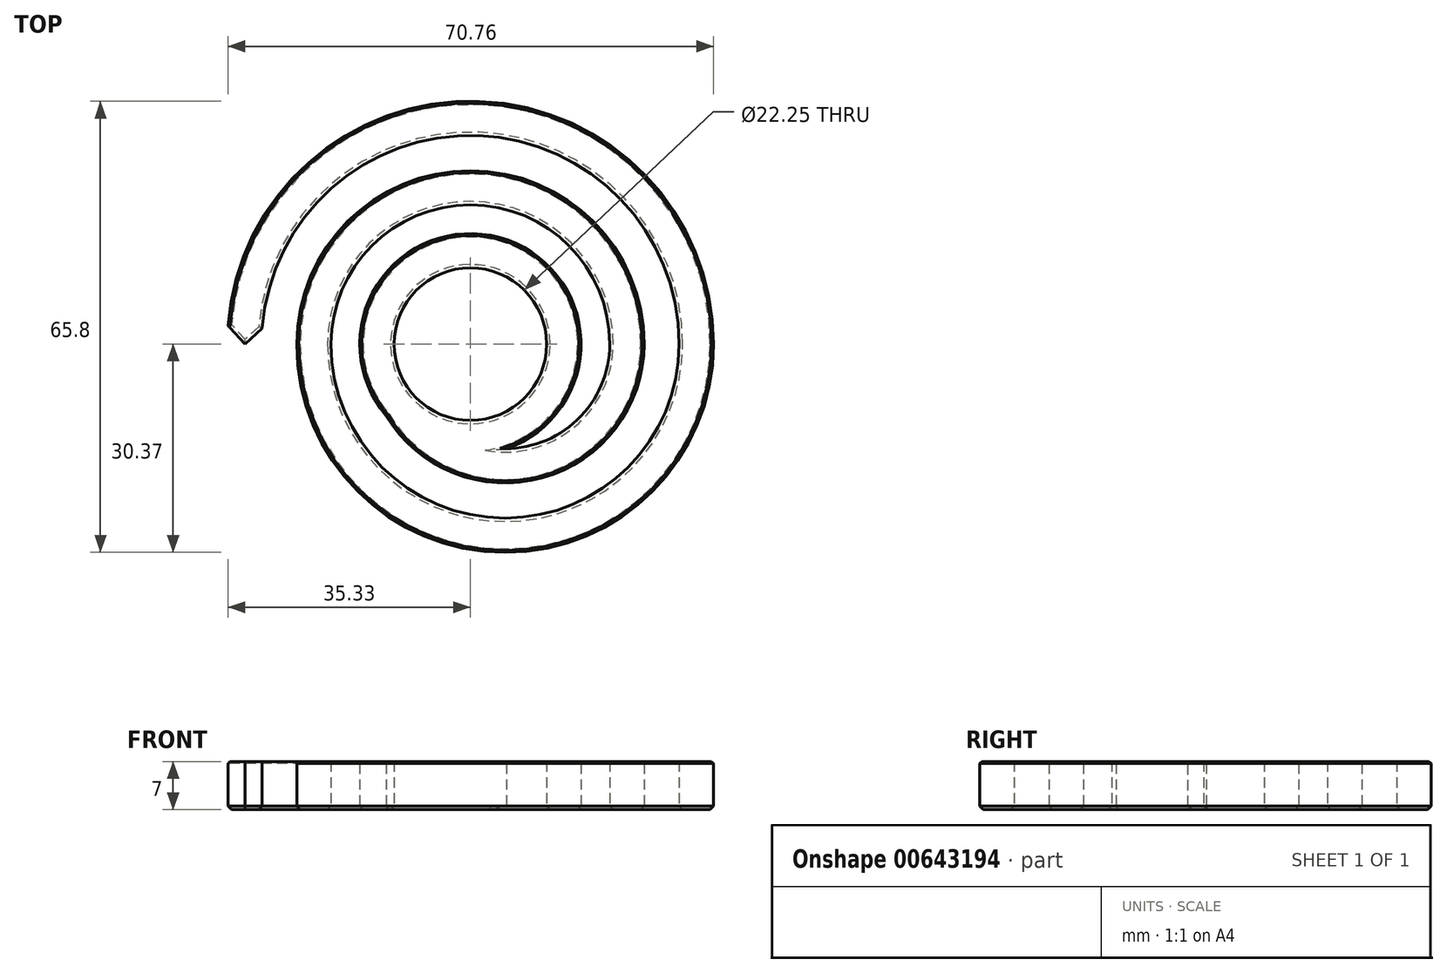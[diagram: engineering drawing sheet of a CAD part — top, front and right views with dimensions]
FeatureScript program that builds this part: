
annotation { "Feature Type Name" : "Feature", "Feature Type Description" : "" }
export const myFeature = defineFeature(function(context is Context, id is Id, definition is map)
    precondition{}
    {
        {
            var Q0;
            Q0=qCreatedBy(makeId("Top.planeOp"),FACE);
            var sketch = newSketch(context, id + "F0", { "sketchPlane" : qUnion([Q0])});
            skCircle(sketch, "E0", {"center": v(0, 0) * mm, "radius": 11.13 * mm});
            skCircle(sketch, "E1", {"center": v(0, 0) * mm, "radius": 16.12 * mm});
            skArc(sketch, "E2", {"start": v(5.06, 0) * mm, "mid": v(0, 5.06) * mm, "end": v(-5.06, 0) * mm});
            skArc(sketch, "E3", {"start": v(-5.06, 0) * mm, "mid": v(5.06, -10.12) * mm, "end": v(15.18, 0) * mm});
            skArc(sketch, "E4", {"start": v(15.18, 0) * mm, "mid": v(0, 15.18) * mm, "end": v(-15.18, 0) * mm});
            skArc(sketch, "E5", {"start": v(-15.18, 0) * mm, "mid": v(5.06, -20.25) * mm, "end": v(25.3, 0) * mm});
            skArc(sketch, "E6", {"start": v(25.3, 0) * mm, "mid": v(0, 25.3) * mm, "end": v(-25.3, 0) * mm});
            skArc(sketch, "E7", {"start": v(-25.3, 0) * mm, "mid": v(5.06, -30.37) * mm, "end": v(35.43, 0) * mm});
            skArc(sketch, "E8", {"start": v(35.43, 0) * mm, "mid": v(0, 35.43) * mm, "end": v(-35.43, 0) * mm});
            skArc(sketch, "E9.0", {"start": v(30.43, 0) * mm, "mid": v(0, 30.43) * mm, "end": v(-30.43, 0) * mm});
            skArc(sketch, "E9.1", {"start": v(-20.3, 0) * mm, "mid": v(5.06, -25.37) * mm, "end": v(30.43, 0) * mm});
            skArc(sketch, "E9.2", {"start": v(20.3, 0) * mm, "mid": v(0, 20.3) * mm, "end": v(-20.3, 0) * mm});
            skArc(sketch, "E9.3", {"start": v(0.06, 0) * mm, "mid": v(0, 0.06) * mm, "end": v(-0.06, 0) * mm});
            skArc(sketch, "E9.4", {"start": v(-0.06, 0) * mm, "mid": v(5.06, -5.12) * mm, "end": v(10.18, 0) * mm});
            skArc(sketch, "E9.5", {"start": v(10.18, 0) * mm, "mid": v(0, 10.18) * mm, "end": v(-10.18, 0) * mm});
            skArc(sketch, "E9.6", {"start": v(-10.18, 0) * mm, "mid": v(5.06, -15.25) * mm, "end": v(20.3, 0) * mm});
            skLineSegment(sketch, "E10", {"start": v(-30.43, 0) * mm, "end": v(-35.43, 0) * mm});
            skSolve(sketch);
        }
        {
            var Q0;
            {var subQ0=sQuery(id+"F0.wireOp",EDGE,"E6");Q0=makeQuery(id+"F0.imprint","IMPRINT",FACE,{"disambiguationData":[TD([[makeQuery(id+"F0.imprint","IMPRINT",EDGE,{"derivedFrom":subQ0}),1.0]])]});}
            var Q1;
            {var subQ0=sQuery(id+"F0.wireOp",EDGE,"E4");Q1=makeQuery(id+"F0.imprint","IMPRINT",FACE,{"disambiguationData":[TD([[makeQuery(id+"F0.imprint","IMPRINT",EDGE,{"derivedFrom":subQ0}),1.0]])]});}
            var Q2;
            {var subQ0=sQuery(id+"F0.wireOp",EDGE,"E4");Q2=makeQuery(id+"F0.imprint","IMPRINT",FACE,{"disambiguationData":[TD([[makeQuery(id+"F0.imprint","IMPRINT",EDGE,{"derivedFrom":subQ0}),-1.0]])]});}
            extrude(context, id + "F1", {"entities" : qUnion([Q0, Q1, Q2]), "depth" : 7 * mm, "offsetDistance" : 25 * mm});
        }
        {
            var Q0;
            Q0=makeQuery(id+"F1.opExtrude","SWEPT_EDGE",EDGE,{"disambiguationData":[OSD([sQuery(id+"F0.wireOp",EDGE,"E8"),sQuery(id+"F0.wireOp",EDGE,"E10")])]});
            var Q1;
            Q1=makeQuery(id+"F1.opExtrude","SWEPT_EDGE",EDGE,{"disambiguationData":[OSD([sQuery(id+"F0.wireOp",EDGE,"E9.0"),sQuery(id+"F0.wireOp",EDGE,"E10")])]});
            chamfer(context, id + "F2", {"entities" : qUnion([Q0, Q1]), "width" : 2.5 * mm, "tangentPropagation" : true});
        }
        {
            var Q0;
            Q0=makeQuery(id+"F1.opExtrude","CAP_EDGE",EDGE,{"disambiguationData":[OSD([sQuery(id+"F0.wireOp",EDGE,"E8")])],"isStart":false});
            var Q1;
            Q1=makeQuery(id+"F1.opExtrude","CAP_EDGE",EDGE,{"disambiguationData":[OSD([sQuery(id+"F0.wireOp",EDGE,"E1")])],"isStart":false});
            chamfer(context, id + "F3", {"entities" : qUnion([Q0, Q1]), "width" : 0.3 * mm, "tangentPropagation" : true});
        }
        {
            var Q0;
            Q0=makeQuery(id+"F1.opExtrude","CAP_FACE",FACE,{"disambiguationData":[OSD([sQuery(id+"F0.wireOp",EDGE,"E0"),sQuery(id+"F0.wireOp",EDGE,"E1"),sQuery(id+"F0.wireOp",EDGE,"E5"),sQuery(id+"F0.wireOp",EDGE,"E6"),sQuery(id+"F0.wireOp",EDGE,"E7"),sQuery(id+"F0.wireOp",EDGE,"E8"),sQuery(id+"F0.wireOp",EDGE,"E9.0"),sQuery(id+"F0.wireOp",EDGE,"E9.1"),sQuery(id+"F0.wireOp",EDGE,"E9.2"),sQuery(id+"F0.wireOp",EDGE,"E9.6"),sQuery(id+"F0.wireOp",EDGE,"E10")])],"isStart":true});
            chamfer(context, id + "F4", {"entities" : qUnion([Q0]), "width" : 0.5 * mm, "tangentPropagation" : true});
        }
    });
